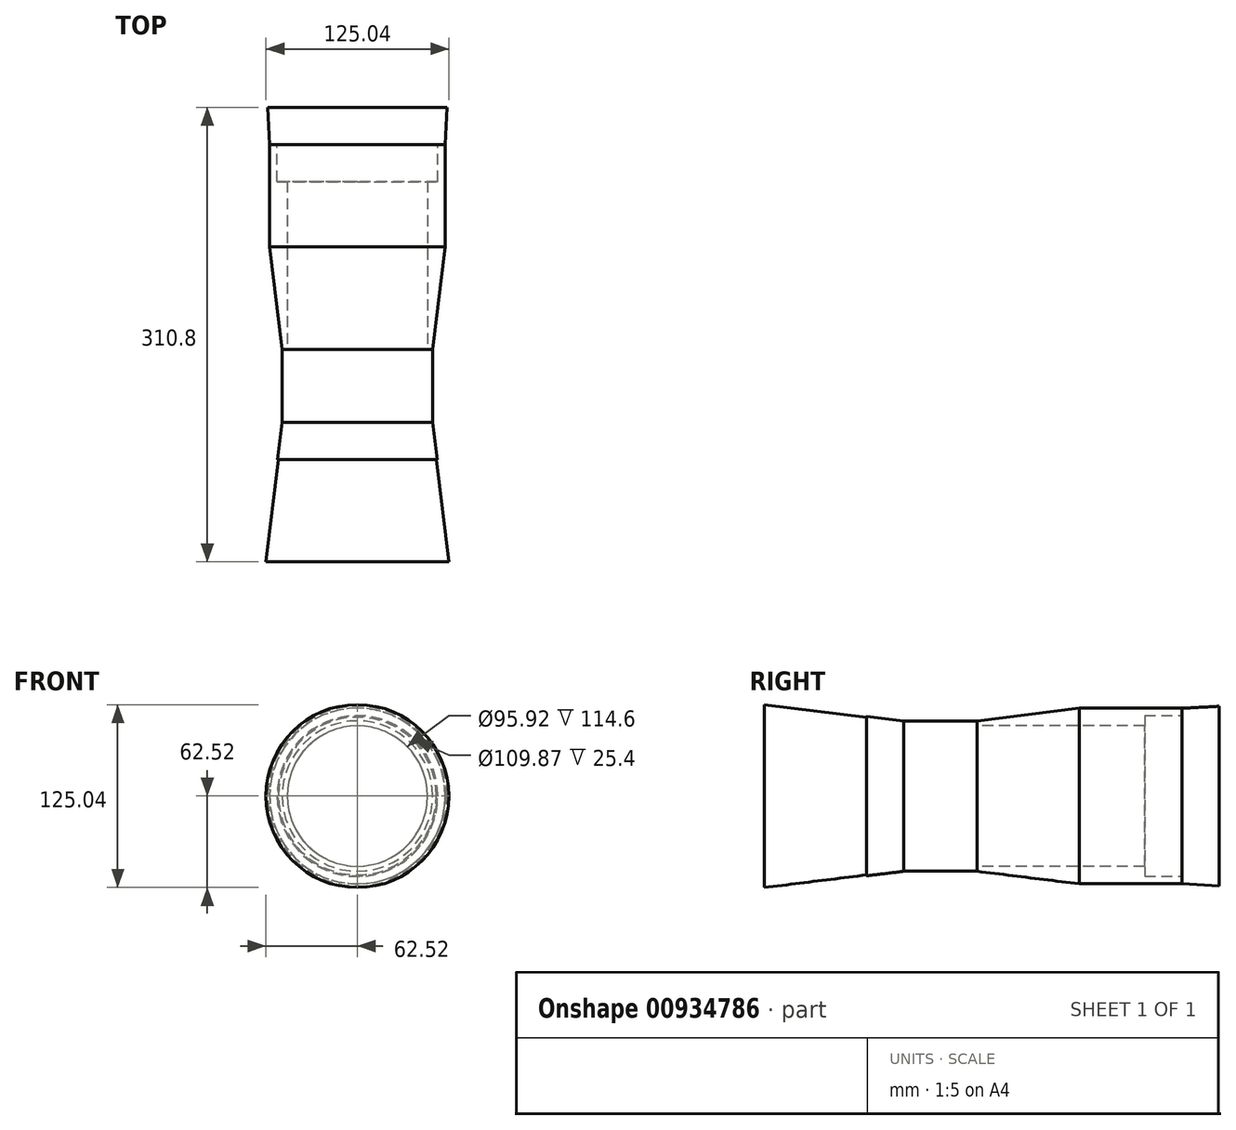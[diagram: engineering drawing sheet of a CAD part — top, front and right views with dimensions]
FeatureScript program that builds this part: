
annotation { "Feature Type Name" : "Feature", "Feature Type Description" : "" }
export const myFeature = defineFeature(function(context is Context, id is Id, definition is map)
    precondition{}
    {
        {
            var Q0;
            Q0=qCreatedBy(makeId("Front.planeOp"),FACE);
            var sketch = newSketch(context, id + "F0", { "sketchPlane" : qUnion([Q0])});
            skCircle(sketch, "E0", {"center": v(0, 0) * mm, "radius": 60 * mm});
            skSolve(sketch);
        }
        {
            var Q0;
            Q0=makeQuery(id+"F0.imprint","IMPRINT",FACE,{"disambiguationData":[TD([[makeQuery(id+"F0.imprint","IMPRINT",EDGE,{"derivedFrom":sQuery(id+"F0.wireOp",EDGE,"E0")}),1.0]])]});
            extrude(context, id + "F1", {"entities" : qUnion([Q0]), "oppositeDirection" : true, "depth" : 70 * mm, "offsetDistance" : 25.4 * mm});
        }
        {
            var Q0;
            Q0=makeQuery(id+"F1.opExtrude","CAP_FACE",FACE,{"disambiguationData":[OSD([sQuery(id+"F0.wireOp",EDGE,"E0")])],"isStart":true});
            var sketch = newSketch(context, id + "F2", { "sketchPlane" : qUnion([Q0])});
            skCircle(sketch, "E1", {"center": v(0, 0) * mm, "radius": 60 * mm});
            skSolve(sketch);
        }
        {
            var Q0;
            Q0=qSketchRegion(id+"F2",true);
            extrude(context, id + "F3", {"entities" : qUnion([Q0]), "operationType" : NewBodyOperationType.ADD, "depth" : 70 * mm, "offsetDistance" : 25.4 * mm, "hasDraft" : true, "draftAngle" : 7 * degree, "draftPullDirection" : true});
        }
        {
            var Q0;
            Q0=makeQuery(id+"F3.opExtrude","CAP_FACE",FACE,{"disambiguationData":[OSD([sQuery(id+"F2.wireOp",EDGE,"E1")])],"isStart":false});
            var sketch = newSketch(context, id + "F4", { "sketchPlane" : qUnion([Q0])});
            skCircle(sketch, "E2", {"center": v(0, 0) * mm, "radius": 53.52 * mm});
            skSolve(sketch);
        }
        {
            var Q0;
            Q0=makeQuery(id+"F1.opExtrude","CAP_FACE",FACE,{"disambiguationData":[OSD([sQuery(id+"F0.wireOp",EDGE,"E0")])],"isStart":false});
            var sketch = newSketch(context, id + "F5", { "sketchPlane" : qUnion([Q0])});
            skCircle(sketch, "E3", {"center": v(0, 0) * mm, "radius": 54.93 * mm});
            skSolve(sketch);
        }
        {
            var Q0;
            Q0=makeQuery(id+"F5.imprint","IMPRINT",FACE,{"disambiguationData":[TD([[makeQuery(id+"F5.imprint","IMPRINT",EDGE,{"derivedFrom":sQuery(id+"F5.wireOp",EDGE,"E3")}),1.0]])]});
            extrude(context, id + "F6", {"entities" : qUnion([Q0]), "operationType" : NewBodyOperationType.REMOVE, "oppositeDirection" : true, "depth" : 25.4 * mm, "offsetDistance" : 25.4 * mm});
        }
        {
            var Q0;
            Q0=makeQuery(id+"F4.imprint","IMPRINT",FACE,{"disambiguationData":[TD([[makeQuery(id+"F4.imprint","IMPRINT",EDGE,{"derivedFrom":sQuery(id+"F4.wireOp",EDGE,"E2")}),1.0]])]});
            var sketch = newSketch(context, id + "F7", { "sketchPlane" : qUnion([Q0])});
            skCircle(sketch, "E4", {"center": v(0, 0) * mm, "radius": 47.96 * mm});
            skSolve(sketch);
        }
        {
            var Q0;
            Q0=qSketchRegion(id+"F7",true);
            extrude(context, id + "F8", {"entities" : qUnion([Q0]), "operationType" : NewBodyOperationType.REMOVE, "oppositeDirection" : true, "depth" : 206 * mm, "offsetDistance" : 25.4 * mm});
        }
        {
            var Q0;
            Q0=makeQuery(id+"F1.opExtrude","CAP_FACE",FACE,{"disambiguationData":[OSD([sQuery(id+"F0.wireOp",EDGE,"E0")])],"isStart":false});
            var sketch = newSketch(context, id + "F9", { "sketchPlane" : qUnion([Q0])});
            skSolve(sketch);
        }
        {
            var Q0;
            Q0=makeQuery(id+"F9.imprint","IMPRINT",FACE,{"disambiguationData":[TD([[makeQuery(id+"F9.imprint","IMPRINT",EDGE,{"derivedFrom":makeQuery(id+"F1.opExtrude","CAP_EDGE",EDGE,{"disambiguationData":[OSD([sQuery(id+"F0.wireOp",EDGE,"E0")])],"isStart":false})}),-1.0]])]});
            var sketch = newSketch(context, id + "F10", { "sketchPlane" : qUnion([Q0])});
            skCircle(sketch, "E5", {"center": v(0, 0) * mm, "radius": 60.8 * mm});
            skSolve(sketch);
        }
        {
            var Q0;
            Q0=makeQuery(id+"F10.imprint","IMPRINT",FACE,{"disambiguationData":[TD([[makeQuery(id+"F10.imprint","IMPRINT",EDGE,{"derivedFrom":sQuery(id+"F10.wireOp",EDGE,"E5")}),1.0]])]});
            var sketch = newSketch(context, id + "F11", { "sketchPlane" : qUnion([Q0])});
            skCircle(sketch, "E6", {"center": v(0, 0) * mm, "radius": 61.4 * mm});
            skSolve(sketch);
        }
        {
            var Q0;
            Q0=makeQuery(id+"F4.imprint","IMPRINT",FACE,{"disambiguationData":[TD([[makeQuery(id+"F4.imprint","IMPRINT",EDGE,{"derivedFrom":makeQuery(id+"F3.opExtrude","CAP_EDGE",EDGE,{"disambiguationData":[OSD([sQuery(id+"F2.wireOp",EDGE,"E1")])],"isStart":false})}),1.0]])]});
            extrude(context, id + "F12", {"entities" : qUnion([Q0]), "operationType" : NewBodyOperationType.ADD, "depth" : 50 * mm, "offsetDistance" : 25.4 * mm});
        }
        {
            var Q0;
            Q0=makeQuery(id+"F12.opExtrude","CAP_FACE",FACE,{"disambiguationData":[OSD([sQuery(id+"F2.wireOp",EDGE,"E1")])],"isStart":false});
            var sketch = newSketch(context, id + "F13", { "sketchPlane" : qUnion([Q0])});
            skSolve(sketch);
        }
        {
            var Q0;
            Q0=makeQuery(id+"F13.imprint","IMPRINT",FACE,{"disambiguationData":[TD([[makeQuery(id+"F13.imprint","IMPRINT",EDGE,{"derivedFrom":makeQuery(id+"F12.opExtrude","CAP_EDGE",EDGE,{"disambiguationData":[OSD([sQuery(id+"F2.wireOp",EDGE,"E1")])],"isStart":false})}),1.0]])]});
            extrude(context, id + "F14", {"entities" : qUnion([Q0]), "operationType" : NewBodyOperationType.ADD, "depth" : 25.4 * mm, "offsetDistance" : 25.4 * mm, "hasDraft" : true, "draftAngle" : 7 * degree});
        }
        {
            var Q0;
            Q0=makeQuery(id+"F14.opExtrude","CAP_FACE",FACE,{"disambiguationData":[OSD([sQuery(id+"F2.wireOp",EDGE,"E1")])],"isStart":false});
            var sketch = newSketch(context, id + "F15", { "sketchPlane" : qUnion([Q0])});
            skCircle(sketch, "E7", {"center": v(0, 0) * mm, "radius": 53.93 * mm});
            skSolve(sketch);
        }
        {
            var Q0;
            Q0=makeQuery(id+"F15.imprint","IMPRINT",FACE,{"disambiguationData":[TD([[makeQuery(id+"F15.imprint","IMPRINT",EDGE,{"derivedFrom":sQuery(id+"F15.wireOp",EDGE,"E7")}),1.0]])]});
            extrude(context, id + "F16", {"entities" : qUnion([Q0]), "operationType" : NewBodyOperationType.ADD, "depth" : 70 * mm, "offsetDistance" : 25.4 * mm, "hasDraft" : true, "draftAngle" : 7 * degree});
        }
        {
            var Q0;
            Q0=makeQuery(id+"F11.imprint","IMPRINT",FACE,{"disambiguationData":[TD([[makeQuery(id+"F11.imprint","IMPRINT",EDGE,{"derivedFrom":makeQuery(id+"F10.imprint","IMPRINT",EDGE,{"derivedFrom":makeQuery(id+"F9.imprint","IMPRINT",EDGE,{"derivedFrom":makeQuery(id+"F1.opExtrude","CAP_EDGE",EDGE,{"disambiguationData":[OSD([sQuery(id+"F0.wireOp",EDGE,"E0")])],"isStart":false})})})}),-1.0]])]});
            extrude(context, id + "F17", {"entities" : qUnion([Q0]), "operationType" : NewBodyOperationType.ADD, "depth" : 25.4 * mm, "offsetDistance" : 25.4 * mm, "hasDraft" : true, "draftAngle" : 3 * degree});
        }
    });
